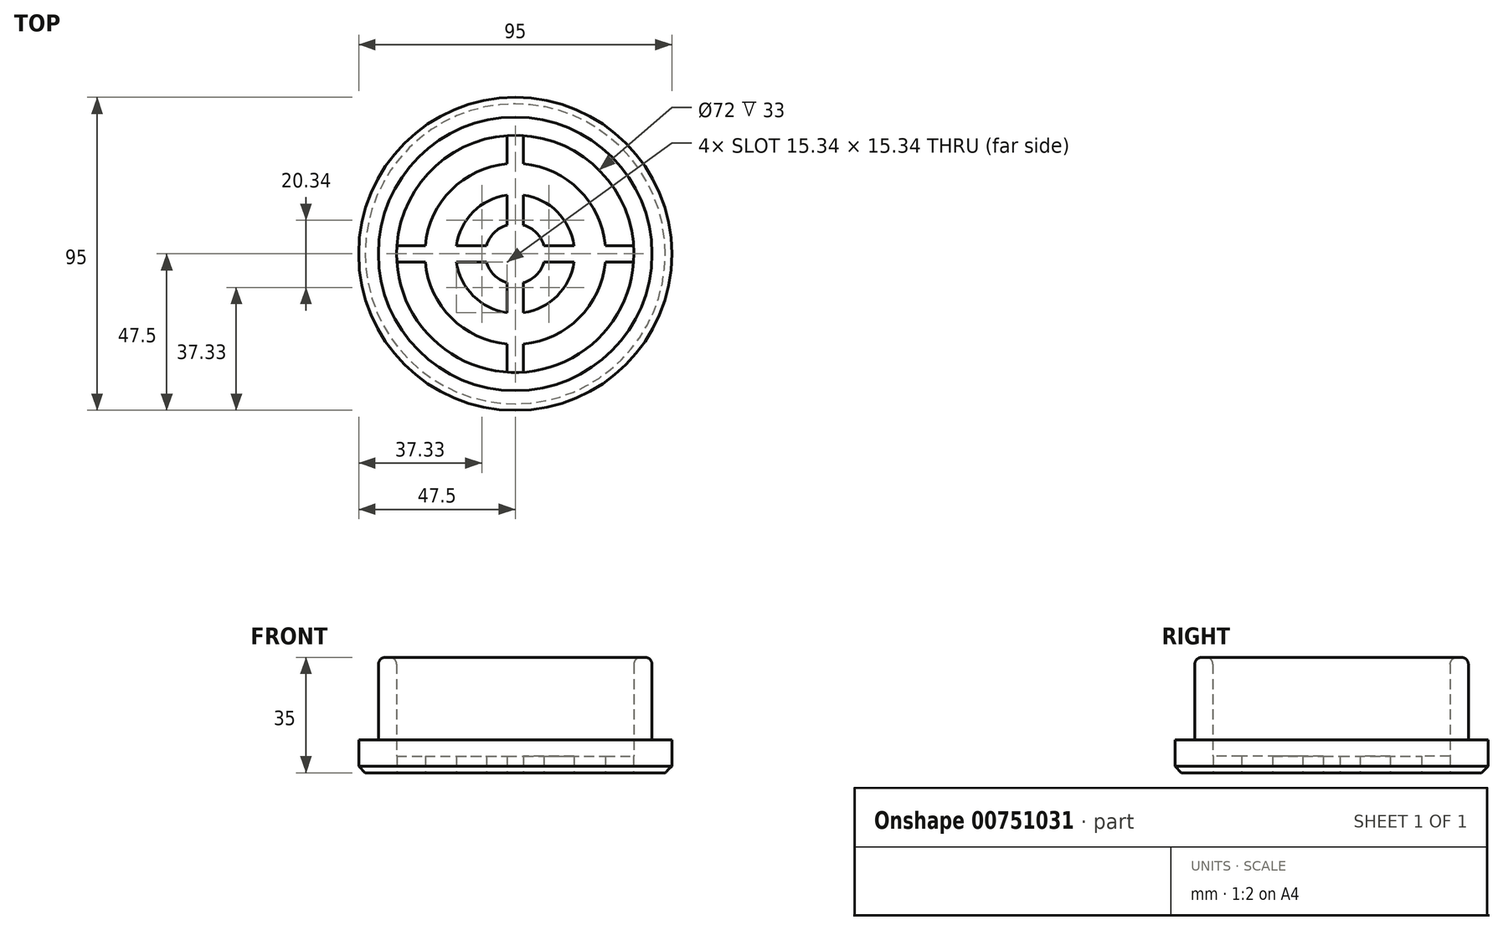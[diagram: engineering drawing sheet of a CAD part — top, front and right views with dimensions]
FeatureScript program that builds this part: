
annotation { "Feature Type Name" : "Feature", "Feature Type Description" : "" }
export const myFeature = defineFeature(function(context is Context, id is Id, definition is map)
    precondition{}
    {
        {
            var Q0;
            Q0=qCreatedBy(makeId("Top.planeOp"),FACE);
            var sketch = newSketch(context, id + "F0", { "sketchPlane" : qUnion([Q0])});
            skCircle(sketch, "E0", {"center": v(0, 0) * mm, "radius": 41.5 * mm});
            skCircle(sketch, "E1", {"center": v(0, 0) * mm, "radius": 47.5 * mm});
            skCircle(sketch, "E2", {"center": v(0, 0) * mm, "radius": 36 * mm});
            skSolve(sketch);
        }
        {
            var Q0;
            Q0=makeQuery(id+"F0.imprint","IMPRINT",FACE,{"disambiguationData":[TD([[makeQuery(id+"F0.imprint","IMPRINT",EDGE,{"derivedFrom":sQuery(id+"F0.wireOp",EDGE,"E0")}),1.0]])]});
            extrude(context, id + "F1", {"entities" : qUnion([Q0]), "depth" : 35 * mm, "offsetDistance" : 25 * mm});
        }
        {
            var Q0;
            Q0=makeQuery(id+"F0.imprint","IMPRINT",FACE,{"disambiguationData":[TD([[makeQuery(id+"F0.imprint","IMPRINT",EDGE,{"derivedFrom":sQuery(id+"F0.wireOp",EDGE,"E0")}),-1.0]])]});
            extrude(context, id + "F2", {"entities" : qUnion([Q0]), "operationType" : NewBodyOperationType.ADD, "depth" : 10 * mm, "offsetDistance" : 25 * mm});
        }
        {
            var Q0;
            Q0=makeQuery(id+"F0.imprint","IMPRINT",FACE,{"disambiguationData":[TD([[makeQuery(id+"F0.imprint","IMPRINT",EDGE,{"derivedFrom":sQuery(id+"F0.wireOp",EDGE,"E2")}),1.0]])]});
            extrude(context, id + "F3", {"entities" : qUnion([Q0]), "operationType" : NewBodyOperationType.ADD, "depth" : 5 * mm, "offsetDistance" : 25 * mm});
        }
        {
            var Q0;
            Q0=makeQuery(id+"F1.opExtrude","CAP_EDGE",EDGE,{"disambiguationData":[OSD([sQuery(id+"F0.wireOp",EDGE,"E0")])],"isStart":false});
            var Q1;
            Q1=makeQuery(id+"F1.opExtrude","CAP_EDGE",EDGE,{"disambiguationData":[OSD([sQuery(id+"F0.wireOp",EDGE,"E2")])],"isStart":false});
            fillet(context, id + "F4", {"entities" : qUnion([Q0, Q1]), "radius" : 2 * mm, "tangentPropagation" : true, "allowEdgeOverflow" : false});
        }
        {
            var Q0;
            Q0=makeQuery(id+"F2.opExtrude","CAP_EDGE",EDGE,{"disambiguationData":[OSD([sQuery(id+"F0.wireOp",EDGE,"E1")])],"isStart":true});
            chamfer(context, id + "F5", {"entities" : qUnion([Q0]), "width" : 2 * mm, "tangentPropagation" : true});
        }
        {
            var Q0;
            Q0=makeQuery(id+"F0.imprint","IMPRINT",FACE,{"disambiguationData":[TD([[makeQuery(id+"F0.imprint","IMPRINT",EDGE,{"derivedFrom":sQuery(id+"F0.wireOp",EDGE,"E2")}),1.0]])]});
            var sketch = newSketch(context, id + "F6", { "sketchPlane" : qUnion([Q0])});
            skLineSegment(sketch, "E3", {"start": v(0, 0) * mm, "end": v(0, -36.11) * mm});
            skLineSegment(sketch, "E4", {"start": v(0, -36.11) * mm, "end": v(0, -18.06) * mm});
            skLineSegment(sketch, "E5", {"start": v(0, 0) * mm, "end": v(0, 35.62) * mm});
            skLineSegment(sketch, "E6", {"start": v(0, 35.62) * mm, "end": v(0, 17.8) * mm});
            skLineSegment(sketch, "E7", {"start": v(0, 0) * mm, "end": v(36.03, 0) * mm});
            skLineSegment(sketch, "E8", {"start": v(36.03, 0) * mm, "end": v(18.01, 0) * mm});
            skLineSegment(sketch, "E9", {"start": v(0, 0) * mm, "end": v(-36.01, 0) * mm});
            skLineSegment(sketch, "E10", {"start": v(-36.01, 0) * mm, "end": v(-18, 0) * mm});
            skCircle(sketch, "E11", {"center": v(0, 0) * mm, "radius": 18.01 * mm});
            skCircle(sketch, "E12", {"center": v(0, 0) * mm, "radius": 9.07 * mm});
            skCircle(sketch, "E13", {"center": v(0, 0) * mm, "radius": 27.42 * mm});
            skLineSegment(sketch, "E14.bottom", {"start": v(2.5, -38.06) * mm, "end": v(-2.5, -38.06) * mm});
            skLineSegment(sketch, "E14.top", {"start": v(2.5, 1.94) * mm, "end": v(-2.5, 1.94) * mm});
            skLineSegment(sketch, "E14.left", {"start": v(2.5, -38.06) * mm, "end": v(2.5, 1.94) * mm});
            skLineSegment(sketch, "E14.right", {"start": v(-2.5, -38.06) * mm, "end": v(-2.5, 1.94) * mm});
            skPoint(sketch, "E14.middle", {"position": v(0, -18.06) * mm});
            skLineSegment(sketch, "E15.bottom", {"start": v(2, -2.5) * mm, "end": v(-38, -2.5) * mm});
            skLineSegment(sketch, "E15.top", {"start": v(2, 2.5) * mm, "end": v(-38, 2.5) * mm});
            skLineSegment(sketch, "E15.left", {"start": v(2, -2.5) * mm, "end": v(2, 2.5) * mm});
            skLineSegment(sketch, "E15.right", {"start": v(-38, -2.5) * mm, "end": v(-38, 2.5) * mm});
            skPoint(sketch, "E15.middle", {"position": v(-18, 0) * mm});
            skLineSegment(sketch, "E16.bottom", {"start": v(2.5, -2.2) * mm, "end": v(-2.5, -2.2) * mm});
            skLineSegment(sketch, "E16.top", {"start": v(2.5, 37.8) * mm, "end": v(-2.5, 37.8) * mm});
            skLineSegment(sketch, "E16.left", {"start": v(2.5, -2.2) * mm, "end": v(2.5, 37.8) * mm});
            skLineSegment(sketch, "E16.right", {"start": v(-2.5, -2.2) * mm, "end": v(-2.5, 37.8) * mm});
            skPoint(sketch, "E16.middle", {"position": v(0, 17.8) * mm});
            skLineSegment(sketch, "E17.bottom", {"start": v(38.01, -2.5) * mm, "end": v(-1.99, -2.5) * mm});
            skLineSegment(sketch, "E17.top", {"start": v(38.01, 2.5) * mm, "end": v(-1.99, 2.5) * mm});
            skLineSegment(sketch, "E17.left", {"start": v(38.01, -2.5) * mm, "end": v(38.01, 2.5) * mm});
            skLineSegment(sketch, "E17.right", {"start": v(-1.99, -2.5) * mm, "end": v(-1.99, 2.5) * mm});
            skPoint(sketch, "E17.middle", {"position": v(18.01, 0) * mm});
            skSolve(sketch);
        }
        {
            var Q0;
            {var subQ0=sQuery(id+"F6.wireOp",EDGE,"E14.left");var subQ1=sQuery(id+"F6.wireOp",EDGE,"E13");var subQ2=makeQuery(id+"F6.imprint","INTERSECT",VERTEX,{"derivedFrom":[subQ1,subQ0]});Q0=makeQuery(id+"F6.imprint","IMPRINT",FACE,{"disambiguationData":[TD([[makeQuery(id+"F6.imprint","IMPRINT",EDGE,{"disambiguationData":[TD([[subQ2,-1.0]])],"derivedFrom":subQ1}),-1.0]])]});}
            var Q1;
            {var subQ0=sQuery(id+"F6.wireOp",EDGE,"E15.bottom");var subQ1=sQuery(id+"F6.wireOp",EDGE,"E13");var subQ2=makeQuery(id+"F6.imprint","INTERSECT",VERTEX,{"derivedFrom":[subQ1,subQ0]});Q1=makeQuery(id+"F6.imprint","IMPRINT",FACE,{"disambiguationData":[TD([[makeQuery(id+"F6.imprint","IMPRINT",EDGE,{"disambiguationData":[TD([[subQ2,-1.0]])],"derivedFrom":subQ1}),-1.0]])]});}
            var Q2;
            {var subQ0=sQuery(id+"F6.wireOp",EDGE,"E16.right");var subQ1=sQuery(id+"F6.wireOp",EDGE,"E13");var subQ2=makeQuery(id+"F6.imprint","INTERSECT",VERTEX,{"derivedFrom":[subQ1,subQ0]});Q2=makeQuery(id+"F6.imprint","IMPRINT",FACE,{"disambiguationData":[TD([[makeQuery(id+"F6.imprint","IMPRINT",EDGE,{"disambiguationData":[TD([[subQ2,-1.0]])],"derivedFrom":subQ1}),-1.0]])]});}
            var Q3;
            {var subQ0=sQuery(id+"F6.wireOp",EDGE,"E17.top");var subQ1=sQuery(id+"F6.wireOp",EDGE,"E13");var subQ2=makeQuery(id+"F6.imprint","INTERSECT",VERTEX,{"derivedFrom":[subQ1,subQ0]});Q3=makeQuery(id+"F6.imprint","IMPRINT",FACE,{"disambiguationData":[TD([[makeQuery(id+"F6.imprint","IMPRINT",EDGE,{"disambiguationData":[TD([[subQ2,-1.0]])],"derivedFrom":subQ1}),-1.0]])]});}
            var Q4;
            {var subQ0=sQuery(id+"F6.wireOp",EDGE,"E17.top");var subQ1=sQuery(id+"F6.wireOp",EDGE,"E11");var subQ2=makeQuery(id+"F6.imprint","INTERSECT",VERTEX,{"derivedFrom":[subQ1,subQ0]});Q4=makeQuery(id+"F6.imprint","IMPRINT",FACE,{"disambiguationData":[TD([[makeQuery(id+"F6.imprint","IMPRINT",EDGE,{"disambiguationData":[TD([[subQ2,-1.0]])],"derivedFrom":subQ1}),1.0]])]});}
            var Q5;
            {var subQ0=sQuery(id+"F6.wireOp",EDGE,"E14.left");var subQ1=sQuery(id+"F6.wireOp",EDGE,"E11");var subQ2=makeQuery(id+"F6.imprint","INTERSECT",VERTEX,{"derivedFrom":[subQ1,subQ0]});Q5=makeQuery(id+"F6.imprint","IMPRINT",FACE,{"disambiguationData":[TD([[makeQuery(id+"F6.imprint","IMPRINT",EDGE,{"disambiguationData":[TD([[subQ2,-1.0]])],"derivedFrom":subQ1}),1.0]])]});}
            var Q6;
            {var subQ0=sQuery(id+"F6.wireOp",EDGE,"E15.bottom");var subQ1=sQuery(id+"F6.wireOp",EDGE,"E11");var subQ2=makeQuery(id+"F6.imprint","INTERSECT",VERTEX,{"derivedFrom":[subQ1,subQ0]});Q6=makeQuery(id+"F6.imprint","IMPRINT",FACE,{"disambiguationData":[TD([[makeQuery(id+"F6.imprint","IMPRINT",EDGE,{"disambiguationData":[TD([[subQ2,-1.0]])],"derivedFrom":subQ1}),1.0]])]});}
            var Q7;
            {var subQ0=sQuery(id+"F6.wireOp",EDGE,"E16.right");var subQ1=sQuery(id+"F6.wireOp",EDGE,"E11");var subQ2=makeQuery(id+"F6.imprint","INTERSECT",VERTEX,{"derivedFrom":[subQ1,subQ0]});Q7=makeQuery(id+"F6.imprint","IMPRINT",FACE,{"disambiguationData":[TD([[makeQuery(id+"F6.imprint","IMPRINT",EDGE,{"disambiguationData":[TD([[subQ2,-1.0]])],"derivedFrom":subQ1}),1.0]])]});}
            extrude(context, id + "F7", {"entities" : qUnion([Q0, Q1, Q2, Q3, Q4, Q5, Q6, Q7]), "operationType" : NewBodyOperationType.REMOVE, "depth" : 40.1 * mm, "offsetDistance" : 25 * mm});
        }
    });
